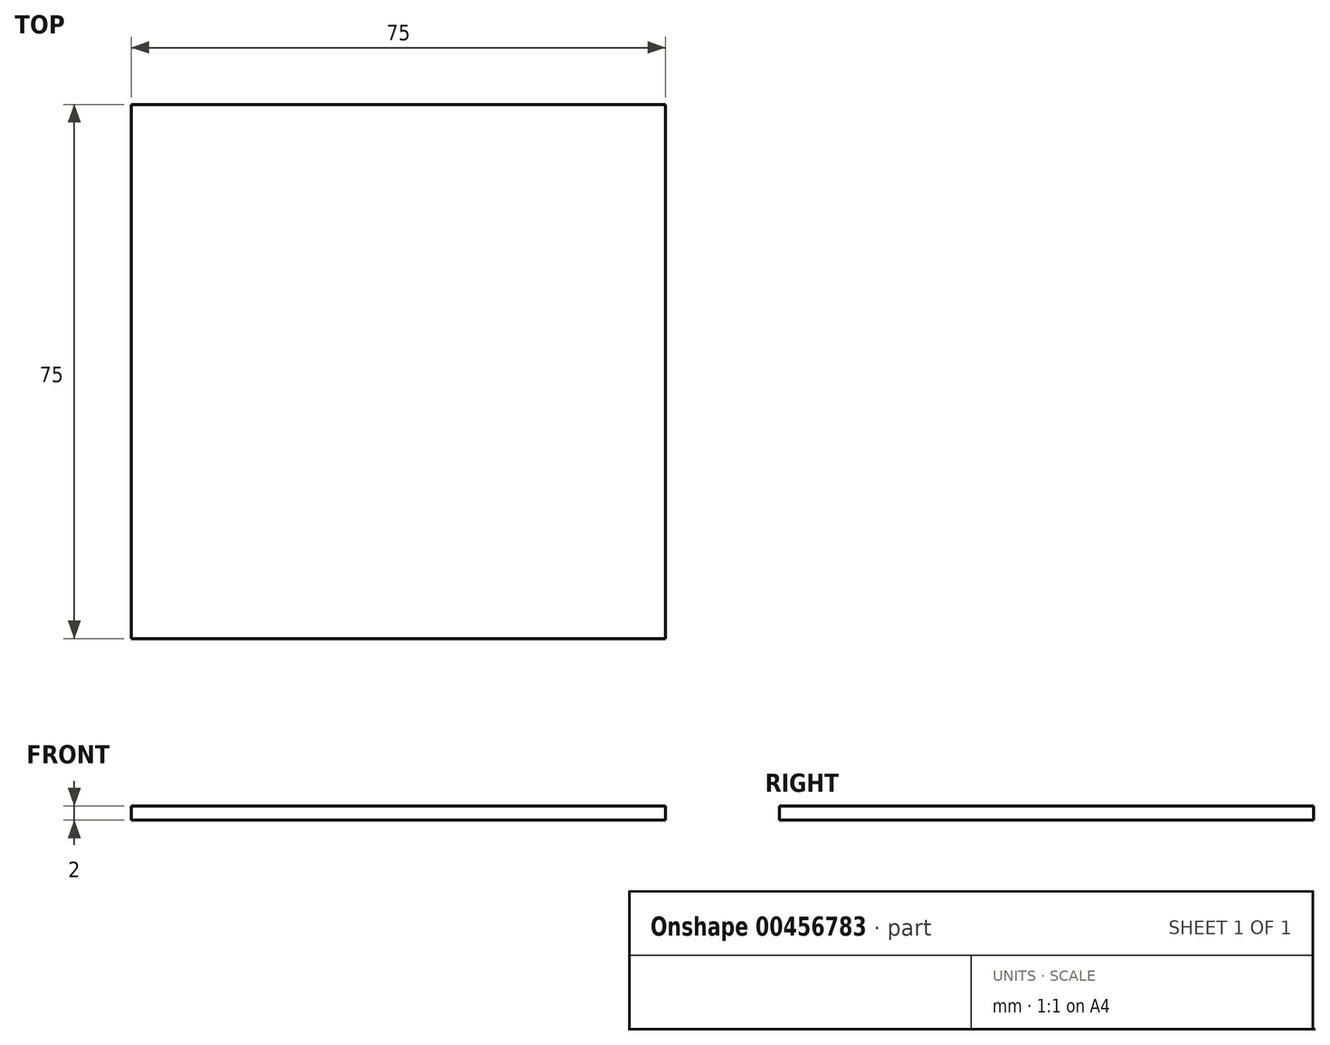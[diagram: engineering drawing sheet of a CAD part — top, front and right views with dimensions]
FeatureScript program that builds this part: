
annotation { "Feature Type Name" : "Feature", "Feature Type Description" : "" }
export const myFeature = defineFeature(function(context is Context, id is Id, definition is map)
    precondition{}
    {
        {
            var Q0;
            Q0=qCreatedBy(makeId("Top.planeOp"),FACE);
            var sketch = newSketch(context, id + "F0", { "sketchPlane" : qUnion([Q0])});
            skLineSegment(sketch, "E0.bottom", {"start": v(0, 0) * mm, "end": v(75, 0) * mm});
            skLineSegment(sketch, "E0.top", {"start": v(0, 75) * mm, "end": v(75, 75) * mm});
            skLineSegment(sketch, "E0.left", {"start": v(0, 0) * mm, "end": v(0, 75) * mm});
            skLineSegment(sketch, "E0.right", {"start": v(75, 0) * mm, "end": v(75, 75) * mm});
            skSolve(sketch);
        }
        {
            var Q0;
            Q0=makeQuery(id+"F0.imprint","IMPRINT",FACE,{"disambiguationData":[TD([[makeQuery(id+"F0.imprint","IMPRINT",EDGE,{"derivedFrom":sQuery(id+"F0.wireOp",EDGE,"E0.bottom")}),1.0]])]});
            extrude(context, id + "F1", {"entities" : qUnion([Q0]), "depth" : 2 * mm});
        }
    });
